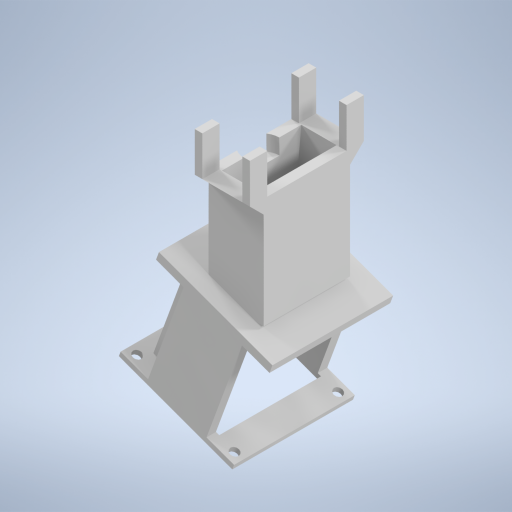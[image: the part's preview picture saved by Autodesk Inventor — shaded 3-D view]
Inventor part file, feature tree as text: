
AUTODESK INVENTOR PART (.ipt)
format: ipt  version: 2024 (Build 280153000, 153)  size: 458,240 bytes
history: native  units: mm
features: sketch x11, extrude x9, other x2, loft x1, plane x1
ambient origin geometry x8: Origin, YZ Plane, XZ Plane, XY Plane, X Axis, Y Axis, Z Axis, Center Point
bodies: Body1 (feature_tree)
feature tree (24):
  other  "Sólido1"
  extrude  "Extrusión1"  Depth=50.0mm
  loft  "Solevación1"
  extrude  "Extrusión2"  Depth=20.5mm
  extrude  "Extrusión3"  TaperAngle=0.0deg  [1 undecoded]
  plane  "Plano de trabajo1"
  extrude  "Extrusión4"  Depth=10.0mm
  extrude  "Extrusión5"  Depth=9.0mm
  extrude  "Extrusión6"  Depth=10.0mm
  extrude  "Extrusión7"  TaperAngle=45.0deg  [1 undecoded]
  extrude  "Extrusión11"  Depth=10.0mm TaperAngle=0.0deg
  extrude  "Extrusión12"  Depth=3.0mm
  sketch  "Boceto1"  dims[d0=32.0mm d1=50.0mm]
  sketch  "Boceto2"  dims[d2=54.0mm d3=0.0mm d4=19.0mm]
  sketch  "Boceto3"  dims[d5=34.0mm d6=20.5mm]
  other  "Aristas1"
  sketch  "Boceto4"  dims[d7=46.0mm d8=0.0mm d9=90.0deg]
  sketch  "Boceto5"  dims[d10=0.0mm d11=90.0deg]
  sketch  "Boceto7"  dims[d12=0.0mm d13=90.0deg d14=0.0mm d15=0.0mm d16=78.75mm d17=10.0mm d18=54.0mm d19=10.0mm d20=51.15mm d21=10.0mm d22=20.5mm]
  sketch  "Boceto8"  dims[d23=9.0mm d24=0.0mm d25=23.2mm]
  sketch  "Boceto9"  dims[d26=0.0mm d27=10.0mm]
  sketch  "Boceto10"  dims[d28=23.0mm d29=0.0mm d30=45.0deg]
  sketch  "Boceto16"  dims[d31=32.0mm d32=0.0mm d33=10.0mm d34=0.0mm]
  sketch  "Boceto18"  dims[d35=10.0mm d36=3.490659mm d37=50.0mm d38=0.0mm d39=70.0mm d40=70.0mm d41=5.0mm d42=0.0mm d73=57.0mm d74=36.0mm d75=0.0mm d76=1.0mm d77=16.0mm d78=8.0mm d79=10.0mm d80=5.0mm d81=1.0mm d82=60.0mm d83=0.0mm d85=0.0mm d86=5.2mm d87=5.2mm d88=5.2mm d89=5.2mm d90=15.0mm d91=3.0mm d92=0.0mm]
note: 2 required parameter values undecoded (feature->parameter linkage not recoverable at this tier; creation-order binding heuristic only, values carry confidence <= 0.55)
